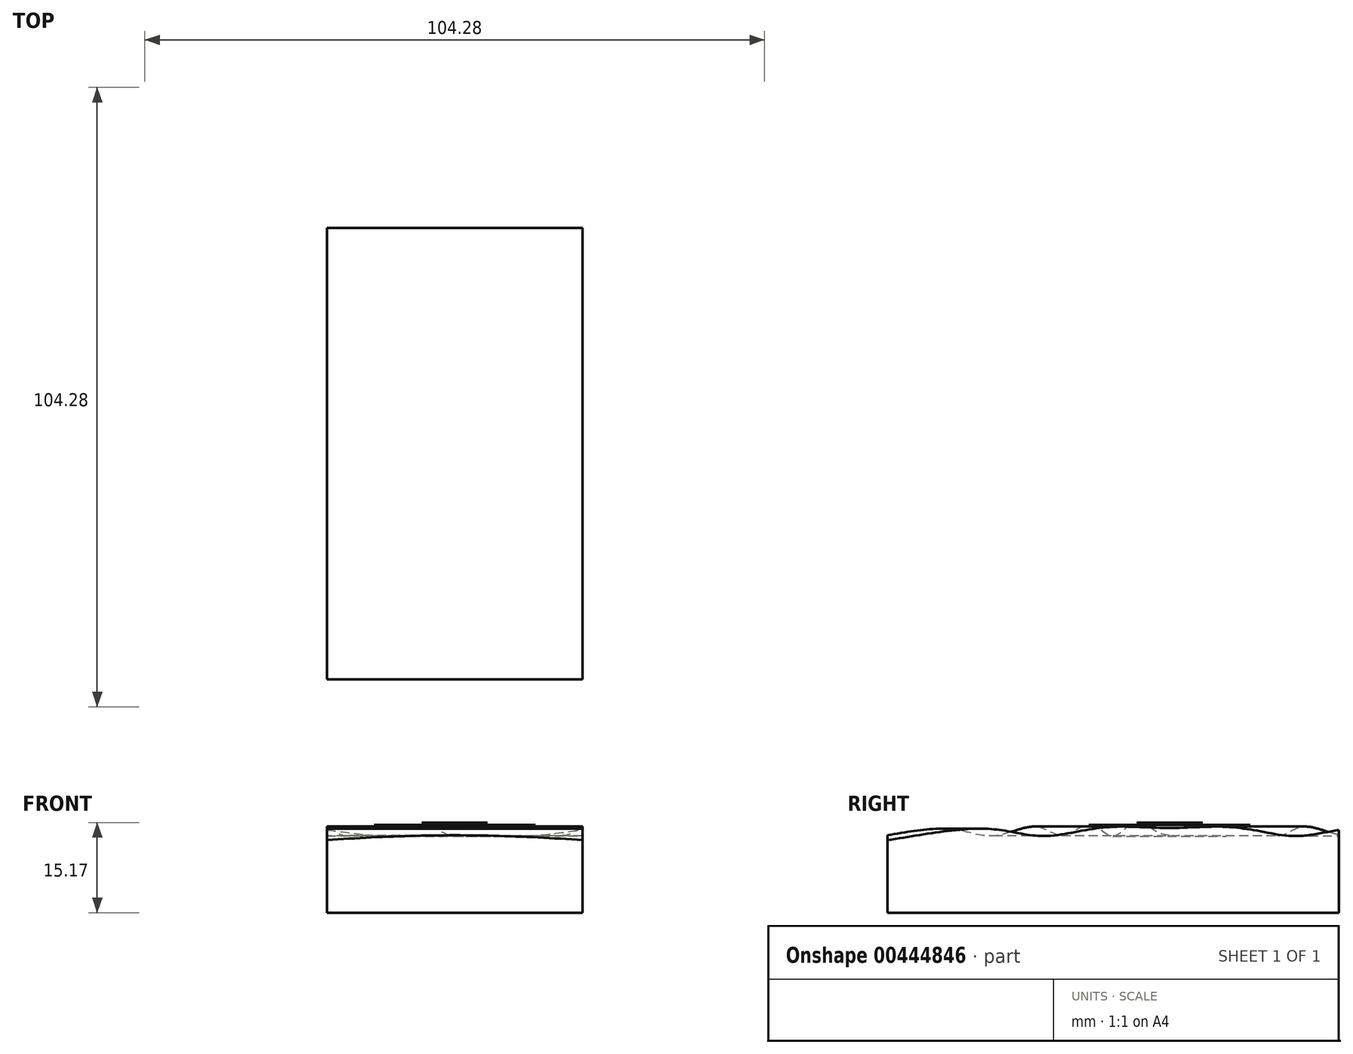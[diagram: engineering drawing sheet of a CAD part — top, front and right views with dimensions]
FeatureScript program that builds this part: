
annotation { "Feature Type Name" : "Feature", "Feature Type Description" : "" }
export const myFeature = defineFeature(function(context is Context, id is Id, definition is map)
    precondition{}
    {
        {
            var Q0;
            Q0=qCreatedBy(makeId("Top.planeOp"),FACE);
            var sketch = newSketch(context, id + "F0", { "sketchPlane" : qUnion([Q0])});
            skLineSegment(sketch, "E0.bottom", {"start": v(-21.5, 38) * mm, "end": v(21.5, 38) * mm});
            skLineSegment(sketch, "E0.top", {"start": v(-21.5, -38) * mm, "end": v(21.5, -38) * mm});
            skLineSegment(sketch, "E0.left", {"start": v(-21.5, 38) * mm, "end": v(-21.5, -38) * mm});
            skLineSegment(sketch, "E0.right", {"start": v(21.5, 38) * mm, "end": v(21.5, -38) * mm});
            skPoint(sketch, "E0.middle", {"position": v(0, 0) * mm});
            skSolve(sketch);
        }
        {
            var Q0;
            Q0 = qSketchRegion(id + "F0", true);
            extrude(context, id + "F1", {"entities" : qUnion([Q0]), "depth" : 12 * mm});
        }
        {
            var Q0;
            Q0=makeQuery(id+"F1.opExtrude","CAP_FACE",FACE,{"disambiguationData":[OSD([sQuery(id+"F0.wireOp",EDGE,"E0.bottom"),sQuery(id+"F0.wireOp",EDGE,"E0.top"),sQuery(id+"F0.wireOp",EDGE,"E0.left"),sQuery(id+"F0.wireOp",EDGE,"E0.right")])],"isStart":false});
            var sketch = newSketch(context, id + "F2", { "sketchPlane" : qUnion([Q0])});
            skLineSegment(sketch, "E1", {"start": v(0, 38) * mm, "end": v(0, 0) * mm});
            skLineSegment(sketch, "E2", {"start": v(0, 0) * mm, "end": v(0, 19) * mm});
            skLineSegment(sketch, "E3", {"start": v(0, 19) * mm, "end": v(0, 9.5) * mm});
            skSolve(sketch);
        }
        {
            var Q0;
            Q0=qCreatedBy(makeId("Right.planeOp"),FACE);
            var sketch = newSketch(context, id + "F3", { "sketchPlane" : qUnion([Q0])});
            skPoint(sketch, "E4.0", {"position": v(9.5, 12) * mm});
            skLineSegment(sketch, "E5", {"start": v(9.5, 12) * mm, "end": v(9.5, 13) * mm});
            skLineSegment(sketch, "E6", {"start": v(9.5, 12) * mm, "end": v(-44.13, 12) * mm});
            skFitSpline(sketch, "E7", {"points": [v(9.5, 13) * mm, v(3.78, 15.16) * mm, v(0, 12.85) * mm, v(-3.85, 14.78) * mm, v(-8.48, 12.98) * mm, v(-12.8, 14.46) * mm, v(-19.92, 12.94) * mm, v(-27.57, 14.09) * mm, v(-44.13, 12) * mm], "startDerivative": vector(-56.8, -0.4) * mm, "endDerivative": vector(-92.6, -13.26) * mm});
            skSolve(sketch);
        }
        {
            var Q0;
            Q0 = qSketchRegion(id + "F3", true);
            var Q1;
            Q1=sQuery(id+"F3.wireOp",EDGE,"E5");
            revolve(context, id + "F4", {"operationType" : NewBodyOperationType.ADD, "entities" : qUnion([Q0]), "axis" : qUnion([Q1]), "revolveType" : RevolveType.FULL});
        }
        {
            var Q0;
            Q0=makeQuery(id+"F4.opRevolve","SWEPT_FACE",FACE,{"disambiguationData":[OSD([sQuery(id+"F3.wireOp",EDGE,"E6")])]});
            extrude(context, id + "F5", {"entities" : qUnion([Q0]), "operationType" : NewBodyOperationType.REMOVE, "oppositeDirection" : true, "depth" : 25 * mm});
        }
    });
